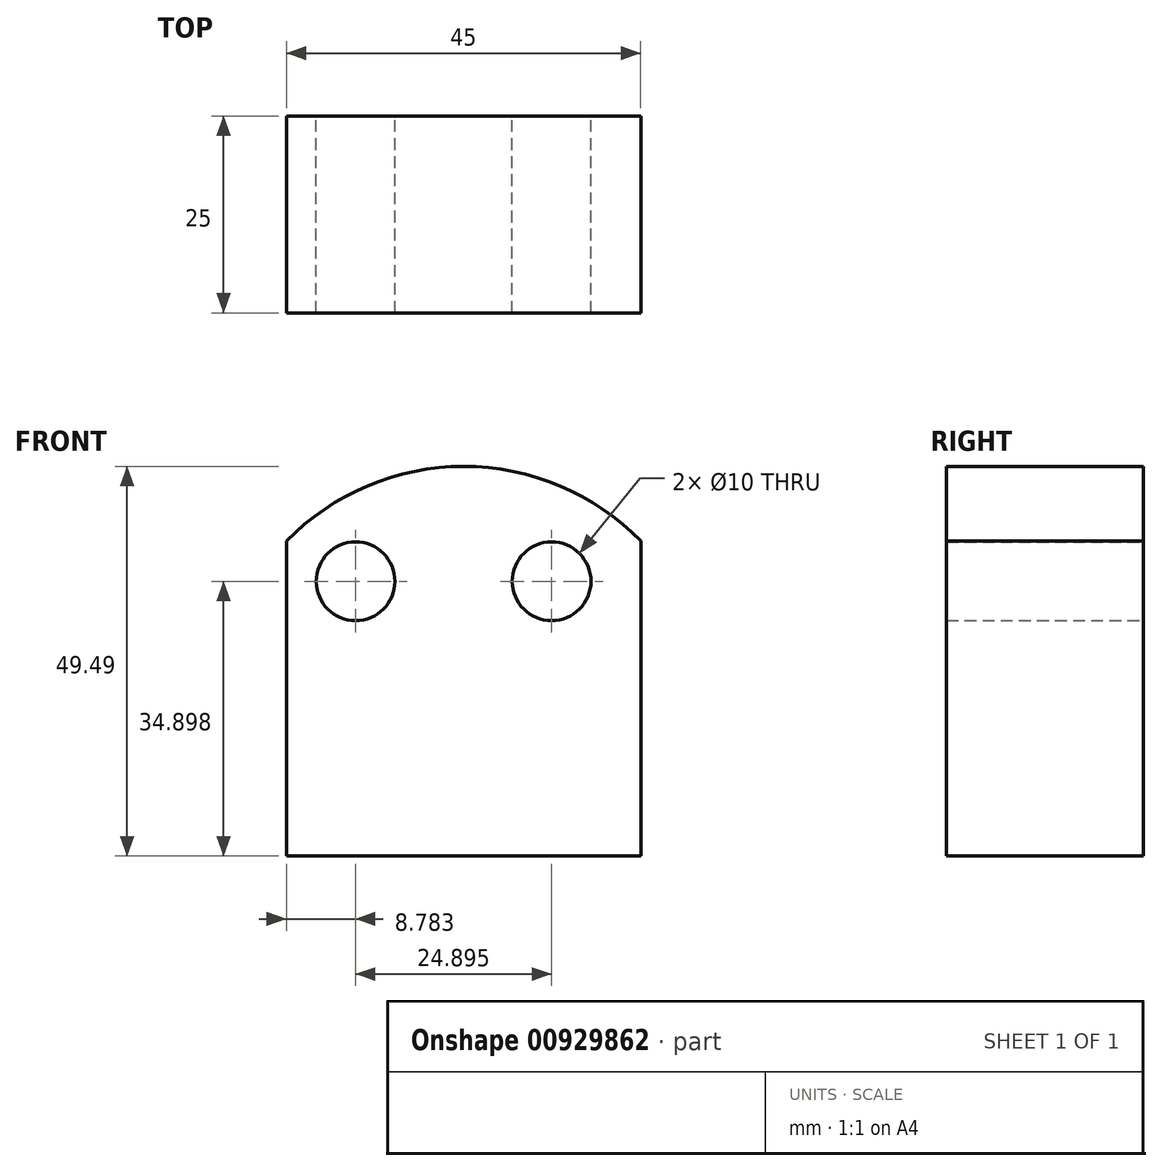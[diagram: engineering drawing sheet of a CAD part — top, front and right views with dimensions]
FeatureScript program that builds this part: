
annotation { "Feature Type Name" : "Feature", "Feature Type Description" : "" }
export const myFeature = defineFeature(function(context is Context, id is Id, definition is map)
    precondition{}
    {
        {
            var Q0;
            Q0=qCreatedBy(makeId("Front.planeOp"),FACE);
            var sketch = newSketch(context, id + "F0", { "sketchPlane" : qUnion([Q0])});
            skLineSegment(sketch, "E0.bottom", {"start": v(-36.03, 31.62) * mm, "end": v(8.97, 31.62) * mm});
            skLineSegment(sketch, "E0.top", {"start": v(-36.03, -8.38) * mm, "end": v(8.97, -8.38) * mm});
            skLineSegment(sketch, "E0.left", {"start": v(-36.03, 31.62) * mm, "end": v(-36.03, -8.38) * mm});
            skLineSegment(sketch, "E0.right", {"start": v(8.97, 31.62) * mm, "end": v(8.97, -8.38) * mm});
            skArc(sketch, "E1", {"start": v(8.97, 31.62) * mm, "mid": v(-13.53, 41.11) * mm, "end": v(-36.03, 31.62) * mm});
            skLineSegment(sketch, "E2", {"start": v(-36.03, 21.62) * mm, "end": v(8.97, 21.62) * mm});
            skCircle(sketch, "E3", {"center": v(-27.25, 26.52) * mm, "radius": 5 * mm});
            skCircle(sketch, "E4", {"center": v(-2.35, 26.52) * mm, "radius": 5 * mm});
            skSolve(sketch);
        }
        {
            var Q0;
            Q0=makeQuery(id+"F0.imprint","IMPRINT",FACE,{"disambiguationData":[TD([[makeQuery(id+"F0.imprint","IMPRINT",EDGE,{"derivedFrom":sQuery(id+"F0.wireOp",EDGE,"E0.bottom")}),1.0]])]});
            var Q1;
            {var subQ2=sQuery(id+"F0.wireOp",EDGE,"E0.bottom");Q1=makeQuery(id+"F0.imprint","IMPRINT",FACE,{"disambiguationData":[TD([[makeQuery(id+"F0.imprint","IMPRINT",EDGE,{"derivedFrom":subQ2}),-1.0]])]});}
            var Q2;
            {var subQ6=sQuery(id+"F0.wireOp",EDGE,"E0.top");Q2=makeQuery(id+"F0.imprint","IMPRINT",FACE,{"disambiguationData":[TD([[makeQuery(id+"F0.imprint","IMPRINT",EDGE,{"derivedFrom":subQ6}),1.0]])]});}
            extrude(context, id + "F1", {"entities" : qUnion([Q0, Q1, Q2]), "depth" : 25 * mm, "offsetDistance" : 25.4 * mm});
        }
    });
